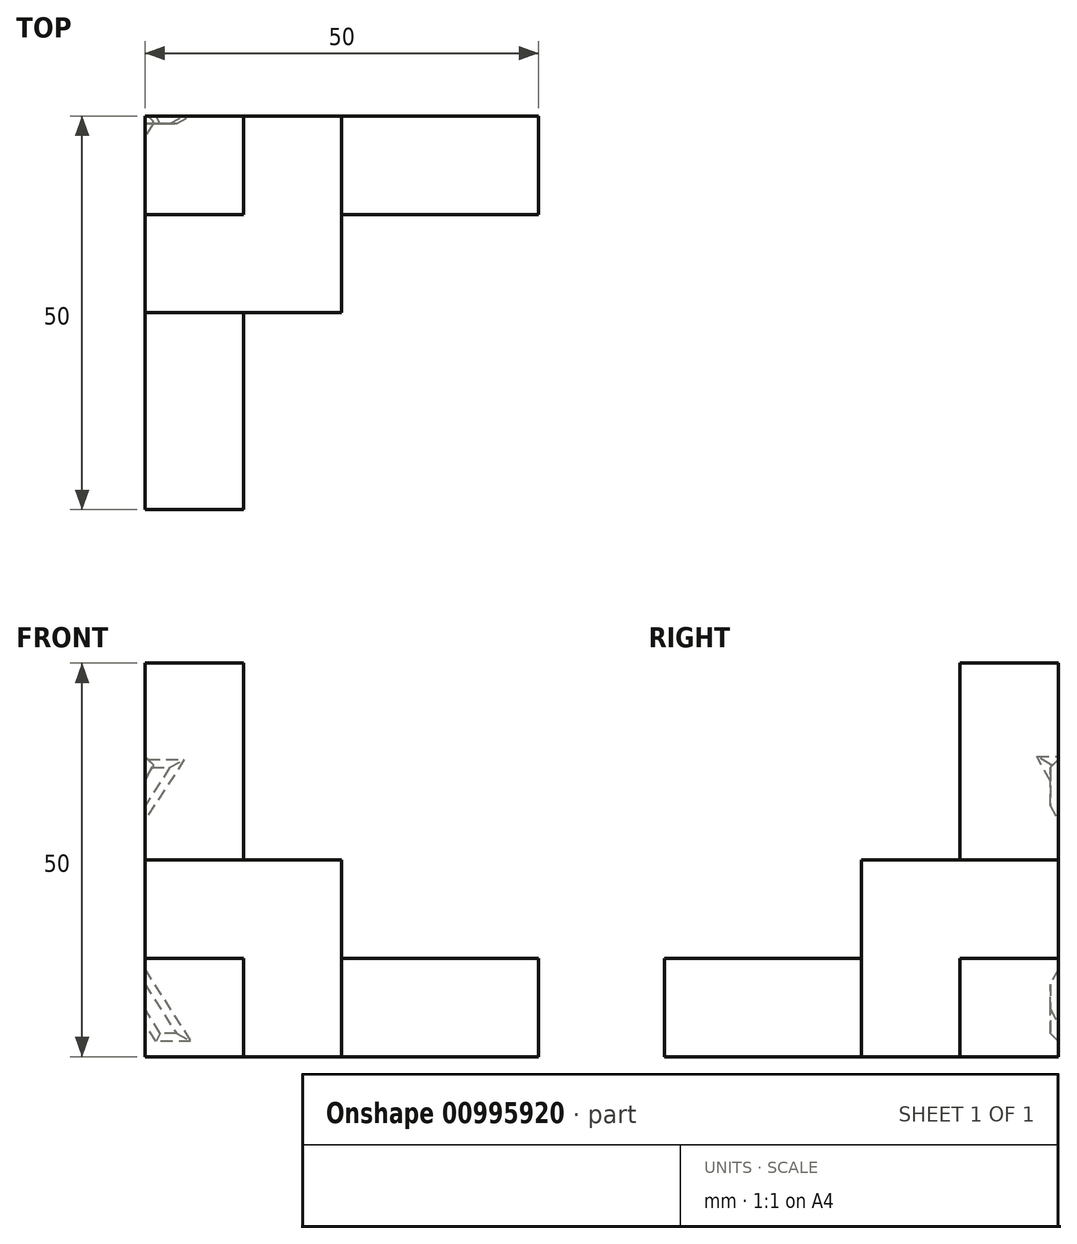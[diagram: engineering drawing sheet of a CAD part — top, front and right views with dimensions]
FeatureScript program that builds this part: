
annotation { "Feature Type Name" : "Feature", "Feature Type Description" : "" }
export const myFeature = defineFeature(function(context is Context, id is Id, definition is map)
    precondition{}
    {
        {
            assignVariable(context, id + "F0", {"name" : "length", "anyValue" : 50});
        }
        {
            var Q0;
            Q0=qCreatedBy(makeId("Top.planeOp"),FACE);
            var sketch = newSketch(context, id + "F1", { "sketchPlane" : qUnion([Q0])});
            skLineSegment(sketch, "E0.bottom", {"start": v(-50, 50) * mm, "end": v(-25, 50) * mm});
            skLineSegment(sketch, "E0.top", {"start": v(-50, 25) * mm, "end": v(-25, 25) * mm});
            skLineSegment(sketch, "E0.left", {"start": v(-50, 50) * mm, "end": v(-50, 25) * mm});
            skLineSegment(sketch, "E0.right", {"start": v(-25, 50) * mm, "end": v(-25, 25) * mm});
            skPoint(sketch, "E1.oppositeSnap0", {"position": v(-25, 37.5) * mm});
            skLineSegment(sketch, "E1.bottom", {"start": v(-50, 50) * mm, "end": v(0, 50) * mm});
            skLineSegment(sketch, "E1.top", {"start": v(-50, 37.5) * mm, "end": v(0, 37.5) * mm});
            skLineSegment(sketch, "E1.left", {"start": v(-50, 50) * mm, "end": v(-50, 37.5) * mm});
            skLineSegment(sketch, "E1.right", {"start": v(0, 50) * mm, "end": v(0, 37.5) * mm});
            skPoint(sketch, "E2.oppositeSnap0", {"position": v(-37.5, 25) * mm});
            skLineSegment(sketch, "E2.bottom", {"start": v(-50, 50) * mm, "end": v(-37.5, 50) * mm});
            skLineSegment(sketch, "E2.top", {"start": v(-50, 0) * mm, "end": v(-37.5, 0) * mm});
            skLineSegment(sketch, "E2.left", {"start": v(-50, 50) * mm, "end": v(-50, 0) * mm});
            skLineSegment(sketch, "E2.right", {"start": v(-37.5, 50) * mm, "end": v(-37.5, 0) * mm});
            skSolve(sketch);
        }
        {
            var Q0;
            {var subQ0=sQuery(id+"F1.wireOp",EDGE,"E2.right");var subQ1=sQuery(id+"F1.wireOp",EDGE,"E0.bottom");var subQ2=makeQuery(id+"F1.imprint","INTERSECT",VERTEX,{"derivedFrom":[subQ1,subQ0]});Q0=makeQuery(id+"F1.imprint","IMPRINT",FACE,{"disambiguationData":[TD([[makeQuery(id+"F1.imprint","IMPRINT",EDGE,{"disambiguationData":[TD([[subQ2,1.0]])],"derivedFrom":subQ1}),-1.0]])]});}
            extrude(context, id + "F2", {"entities" : qUnion([Q0]), "depth" : (getVariable(context, 'length')) * mm, "offsetDistance" : 25 * mm});
        }
        {
            var Q0;
            {var subQ3=sQuery(id+"F1.wireOp",EDGE,"E2.right");var subQ5=sQuery(id+"F1.wireOp",EDGE,"E1.top");var subQ7=makeQuery(id+"F1.imprint","INTERSECT",VERTEX,{"derivedFrom":[subQ5,subQ3]});Q0=makeQuery(id+"F1.imprint","IMPRINT",FACE,{"disambiguationData":[TD([[makeQuery(id+"F1.imprint","IMPRINT",EDGE,{"disambiguationData":[TD([[subQ7,1.0]])],"derivedFrom":subQ5}),-1.0]])]});}
            var Q1;
            {var subQ0=sQuery(id+"F1.wireOp",EDGE,"E0.right");var subQ1=sQuery(id+"F1.wireOp",EDGE,"E0.top");var subQ2=makeQuery(id+"F1.imprint","INTERSECT",VERTEX,{"derivedFrom":[subQ1,subQ0]});Q1=makeQuery(id+"F1.imprint","IMPRINT",FACE,{"disambiguationData":[TD([[makeQuery(id+"F1.imprint","IMPRINT",EDGE,{"disambiguationData":[TD([[subQ2,1.0]])],"derivedFrom":subQ1}),1.0]])]});}
            var Q2;
            {var subQ3=sQuery(id+"F1.wireOp",EDGE,"E0.right");var subQ5=sQuery(id+"F1.wireOp",EDGE,"E1.top");var subQ6=makeQuery(id+"F1.imprint","INTERSECT",VERTEX,{"derivedFrom":[subQ3,subQ5]});Q2=makeQuery(id+"F1.imprint","IMPRINT",FACE,{"disambiguationData":[TD([[makeQuery(id+"F1.imprint","IMPRINT",EDGE,{"disambiguationData":[TD([[subQ6,1.0]])],"derivedFrom":subQ5}),1.0]])]});}
            extrude(context, id + "F3", {"entities" : qUnion([Q0, Q1, Q2]), "operationType" : NewBodyOperationType.ADD, "depth" : (getVariable(context, 'length') / 2) * mm, "offsetDistance" : 25 * mm});
        }
        {
            var Q0;
            {var subQ0=sQuery(id+"F1.wireOp",EDGE,"E2.right");var subQ1=sQuery(id+"F1.wireOp",EDGE,"E0.bottom");var subQ2=makeQuery(id+"F1.imprint","INTERSECT",VERTEX,{"derivedFrom":[subQ1,subQ0]});var subQ5=sQuery(id+"F1.wireOp",EDGE,"E1.top");var subQ7=makeQuery(id+"F1.imprint","INTERSECT",VERTEX,{"derivedFrom":[subQ5,subQ0]});var subQ8=makeQuery(id+"F1.imprint","IMPRINT",EDGE,{"disambiguationData":[TD([[subQ7,1.0]])],"derivedFrom":subQ5});var subQ11=sQuery(id+"F1.wireOp",EDGE,"E0.top");var subQ16=sQuery(id+"F1.wireOp",EDGE,"E1.bottom");var subQ17=sQuery(id+"F1.wireOp",EDGE,"E0.right");var subQ19=makeQuery(id+"F1.imprint","INTERSECT",VERTEX,{"derivedFrom":[subQ17,subQ5]});var subQ22=makeQuery(id+"F1.imprint","IMPRINT",EDGE,{"disambiguationData":[TD([[subQ19,1.0]])],"derivedFrom":subQ5});var subQ23=sQuery(id+"F1.wireOp",EDGE,"E2.top");var subQ24=makeQuery(id+"F1.imprint","INTERSECT",VERTEX,{"derivedFrom":[subQ11,subQ17]});Q0=qUnion([makeQuery(id+"F1.imprint","IMPRINT",FACE,{"disambiguationData":[TD([[makeQuery(id+"F1.imprint","IMPRINT",EDGE,{"disambiguationData":[TD([[subQ24,1.0]])],"derivedFrom":subQ11}),1.0]])]}),makeQuery(id+"F1.imprint","IMPRINT",FACE,{"disambiguationData":[TD([[makeQuery(id+"F1.imprint","IMPRINT",EDGE,{"derivedFrom":subQ23}),1.0]])]}),makeQuery(id+"F1.imprint","IMPRINT",FACE,{"disambiguationData":[TD([[subQ22,1.0]])]}),makeQuery(id+"F1.imprint","IMPRINT",FACE,{"disambiguationData":[TD([[makeQuery(id+"F1.imprint","IMPRINT",EDGE,{"derivedFrom":subQ16}),-1.0]])]}),makeQuery(id+"F1.imprint","IMPRINT",FACE,{"disambiguationData":[TD([[subQ8,-1.0]])]}),makeQuery(id+"F1.imprint","IMPRINT",FACE,{"disambiguationData":[TD([[makeQuery(id+"F1.imprint","IMPRINT",EDGE,{"disambiguationData":[TD([[subQ2,1.0]])],"derivedFrom":subQ1}),-1.0]])]})]);}
            extrude(context, id + "F4", {"entities" : qUnion([Q0]), "operationType" : NewBodyOperationType.ADD, "depth" : (getVariable(context, 'length') / 4) * mm, "offsetDistance" : 25 * mm});
        }
        {
            var Q0;
            {var subQ0=sQuery(id+"F1.wireOp",EDGE,"E0.bottom");Q0=makeQuery(id+"F4.boolean.opBoolean","MERGE",FACE,{"derivedFrom":[makeQuery(id+"F3.boolean.opBoolean","MERGE",FACE,{"derivedFrom":[makeQuery(id+"F2.opExtrude","SWEPT_FACE",FACE,{"disambiguationData":[OSD([subQ0])]}),makeQuery(id+"F3.opExtrude","SWEPT_FACE",FACE,{"disambiguationData":[OSD([subQ0])]})]}),makeQuery(id+"F4.opExtrude","SWEPT_FACE",FACE,{"disambiguationData":[OSD([subQ0,sQuery(id+"F1.wireOp",EDGE,"E1.bottom")])]})]});}
            var sketch = newSketch(context, id + "F5", { "sketchPlane" : qUnion([Q0])});
            skText(sketch, "E3", { "text": "X", "fontName": "OpenSans-Regular.ttf"});
            skLineSegment(sketch, "E4", {"start": v(29, 22.1) * mm, "end": v(29, 25) * mm, "construction": true});
            skLineSegment(sketch, "E5", {"start": v(29, 2.9) * mm, "end": v(29, 0) * mm, "construction": true});
            skLineSegment(sketch, "E6", {"start": v(29, 22.1) * mm, "end": v(25, 22.1) * mm, "construction": true});
            skLineSegment(sketch, "E7", {"start": v(46, 22.1) * mm, "end": v(50, 22.1) * mm, "construction": true});
            const initialGuessF5  = {"E3": [0.044, 0.00195, 1, 0, 0.0361]};
            skSetInitialGuess(sketch, initialGuessF5);
            skSolve(sketch);
        }
        {
            var Q0;
            {var subQ0=sQuery(id+"F1.wireOp",EDGE,"E0.left");Q0=makeQuery(id+"F4.boolean.opBoolean","MERGE",FACE,{"derivedFrom":[makeQuery(id+"F3.boolean.opBoolean","MERGE",FACE,{"derivedFrom":[makeQuery(id+"F2.opExtrude","SWEPT_FACE",FACE,{"disambiguationData":[OSD([subQ0])]}),makeQuery(id+"F3.opExtrude","SWEPT_FACE",FACE,{"disambiguationData":[OSD([subQ0])]})]}),makeQuery(id+"F4.opExtrude","SWEPT_FACE",FACE,{"disambiguationData":[OSD([subQ0,sQuery(id+"F1.wireOp",EDGE,"E2.left")])]})]});}
            var sketch = newSketch(context, id + "F6", { "sketchPlane" : qUnion([Q0])});
            skText(sketch, "E8", { "text": "Y", "fontName": "OpenSans-Regular.ttf"});
            skLineSegment(sketch, "E9", {"start": v(-46, 22.3) * mm, "end": v(-46, 25) * mm, "construction": true});
            skLineSegment(sketch, "E10", {"start": v(-46, 2.7) * mm, "end": v(-46, 0) * mm, "construction": true});
            skLineSegment(sketch, "E11", {"start": v(-46, 22.3) * mm, "end": v(-50, 22.3) * mm, "construction": true});
            skLineSegment(sketch, "E12", {"start": v(-29, 22.3) * mm, "end": v(-25, 22.3) * mm, "construction": true});
            const initialGuessF6  = {"E8": [-0.076, 0.00156, 1, 0, 0.03687]};
            skSetInitialGuess(sketch, initialGuessF6);
            skSolve(sketch);
        }
        {
            var Q0;
            Q0 = qSketchRegion(id + "F5", true);
            extrude(context, id + "F7", {"entities" : qUnion([Q0]), "operationType" : NewBodyOperationType.REMOVE, "oppositeDirection" : true, "depth" : 1 * mm, "offsetDistance" : 25 * mm, "hasDraft" : true, "draftAngle" : 45 * degree, "draftPullDirection" : true});
        }
        {
            var Q0;
            Q0 = qSketchRegion(id + "F6", true);
            extrude(context, id + "F8", {"entities" : qUnion([Q0]), "operationType" : NewBodyOperationType.REMOVE, "oppositeDirection" : true, "depth" : 1 * mm, "offsetDistance" : 25 * mm, "hasDraft" : true, "draftAngle" : 45 * degree, "draftPullDirection" : true});
        }
    });
